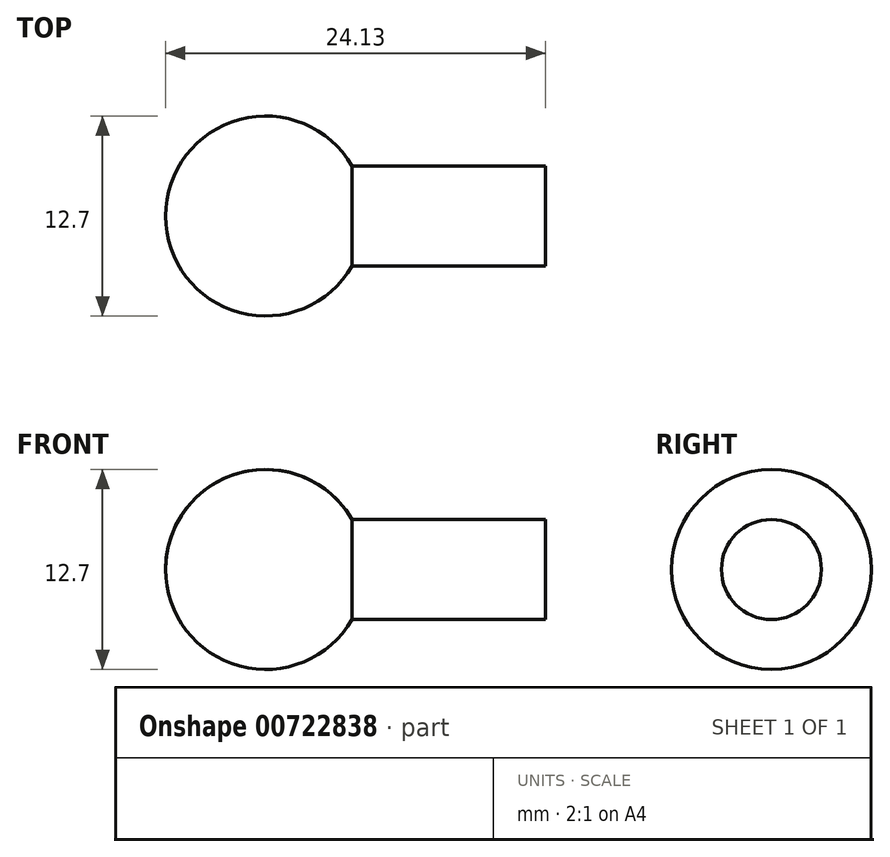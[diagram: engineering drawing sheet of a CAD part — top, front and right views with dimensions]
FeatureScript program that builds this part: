
annotation { "Feature Type Name" : "Feature", "Feature Type Description" : "" }
export const myFeature = defineFeature(function(context is Context, id is Id, definition is map)
    precondition{}
    {
        {
            var Q0;
            Q0=qCreatedBy(makeId("Front.planeOp"),FACE);
            var sketch = newSketch(context, id + "F0", { "sketchPlane" : qUnion([Q0])});
            skArc(sketch, "E0", {"start": v(-6.35, 0) * mm, "mid": v(-1.64, -6.13) * mm, "end": v(5.5, -3.17) * mm});
            skLineSegment(sketch, "E1.top", {"start": v(5.5, -3.17) * mm, "end": v(17.78, -3.17) * mm});
            skLineSegment(sketch, "E1.right", {"start": v(17.78, 0) * mm, "end": v(17.78, -3.17) * mm});
            skPoint(sketch, "E1.left.start.orphan", {"position": v(0, 3.18) * mm});
            skLineSegment(sketch, "E2", {"start": v(17.78, 0) * mm, "end": v(-6.35, 0) * mm});
            skSolve(sketch);
        }
        {
            var Q0;
            Q0=makeQuery(id+"F0.imprint","IMPRINT",FACE,{"disambiguationData":[TD([[makeQuery(id+"F0.imprint","IMPRINT",EDGE,{"derivedFrom":sQuery(id+"F0.wireOp",EDGE,"E0")}),1.0]])]});
            var Q1;
            Q1=sQuery(id+"F0.wireOp",EDGE,"E2");
            revolve(context, id + "F1", {"surfaceOperationType" : NewSurfaceOperationType.NEW, "entities" : qUnion([Q0]), "axis" : qUnion([Q1]), "revolveType" : RevolveType.FULL});
        }
    });
